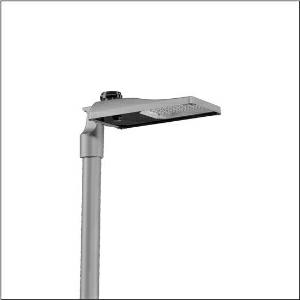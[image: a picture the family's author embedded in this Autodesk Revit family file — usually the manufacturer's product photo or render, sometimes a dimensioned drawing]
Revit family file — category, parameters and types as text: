
# Revit family: streetlight_sl_31_mini___st1_0a_5xh2d3bm08ga_d23b
name_source: partatom
category: Lighting Fixtures
units: mm (PartAtom-declared; Revit-internal decimal feet)

## family parameters
Cut with Voids When Loaded = No
Host = Face
Light Source = No
Part Type = Normal
Room Calculation Point = No
Round Connector Dimension = Use Diameter
Shared = No

## types (1)
- --- (1 x LED, 5880 lm, 39.3 W, 3000K)
    Apparent Load = 39 VA
    CIE Flux Codes = 37 72 97 100 100
    Color Rendering = 70
    Color Temperature = 3000K
    Default Elevation = 1800 mm
    Description = Streetlight SL 31 mini NEMA (7pin) mast luminaire for post-top, side-entry; light control with lens of PMMA; light distribution: ST1.0a, direct asymmetric distribution, for standard-compliant lighting for roads and squares; LED: luminous flux: 5.880lm, light colour: 730, colour temperature: 3000K; luminous efficacy: 149,6lm/W; control: pre-setting: linear dimming characteristic, flexible luminous flux parameterisation, time-dependent luminous flux control, constant luminous flux control, intelligent temperature release in ECG and LED module, overheat protection; luminaire housing, of diecast aluminium, SITECO metallic grey (DB 702S), corrosivity category C5 high according to DIN EN ISO 12944; cover of toughened safety glass, transparent, mast flange of diecast aluminium, SITECO metallic grey (DB 702S), spigot size: 76/60mm, mast flange included unmounted; cable length: 6,5m, connection cable pre-assembled; mains connection: 220..240V, AC, 50/60Hz; power consumption (at start of service life): 39,3W / (at end of service life): 40,7W / (with reduced operation 50%): 18,1W; protection rating (complete): IP66; insulation class (complete): insulation class I (protective earthing); impact resistance: IK09; certification: CE, ENEC, ENEC+, VDE, UKCA; permissible operating ambient temperature for outdoor applications: -40..+50°C; packaging unit: 1 piece

Light Distribution: ST1.0a
    Height = 76 mm
    Lamp = 1 x LED
    Lamp Light Flux = 5880 lm
    Lamp Power = 39.3 W
    Lamp count = 1
    Length = 547 mm
    Luminous efficacy = 150 lm/W
    Manufacturer = Siteco
    ModVariant = No
    Model = 5XH2D3BM08GA
    Number of Poles = 1
    OnlyDefault = Yes
    Power Factor = 1
    Product Name = Streetlight SL 31 mini | ST1.0a
    Product group = mast luminaire | pylon top
    ProductGroupID = 6100
    Protection Class = Protection class I
    Protection Degree = IP 66
    RLX_Detail_Level = 1
    RLX_Emergency_Light_Flux = 0 lm
    RLX_Emergency_Type = 0
    RLX_Emergency_Type_DB = No
    RlxData = <blob elided: 40217 chars, md5=bd249c2c>
    Socket = socket
    Standby Power = 0 W
    System Light Flux = 5880 lm
    System Power = 39 W
    Type Comments = factory setting: luminous flux: 100 % | dim-lin: 254 | 798 mA
    Type Image = l_1300324.jpg
    URL = http://relux.com
    VarID = @adj_061137
    Voltage = 0 V
    Weight = 0.00 kg
    Width = 265 mm

## geometry (parser evidence)
native form markers: Blend x4, Sweep x10
no freeform markers — native parametric forms only
